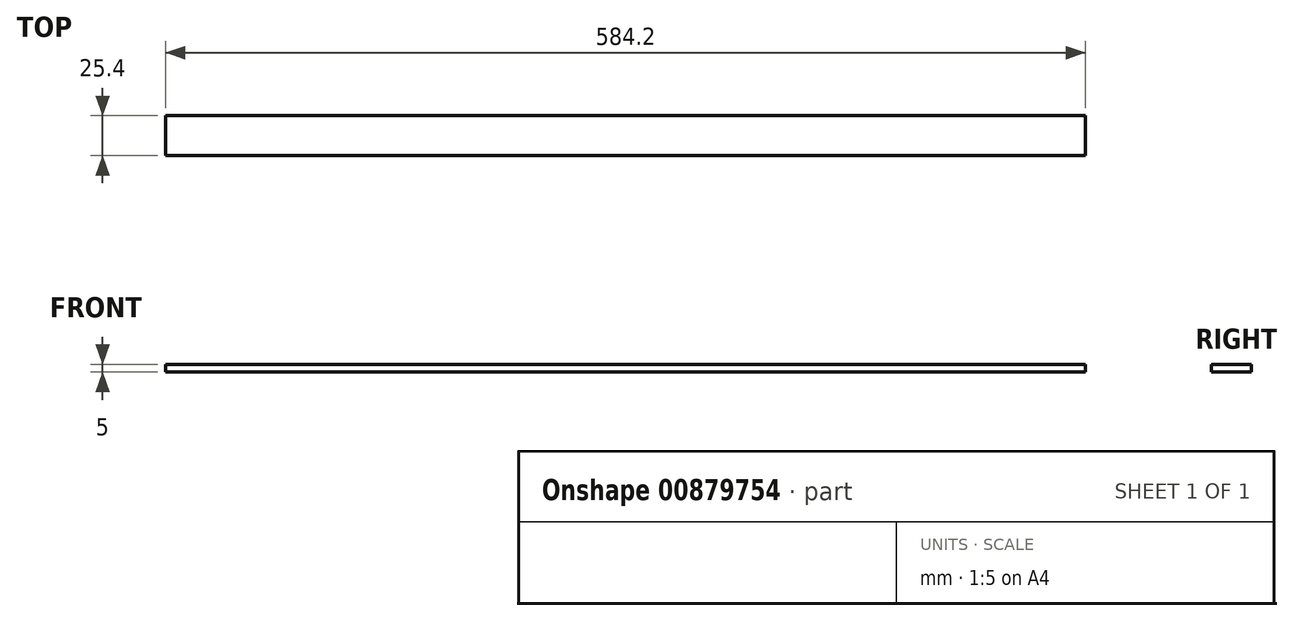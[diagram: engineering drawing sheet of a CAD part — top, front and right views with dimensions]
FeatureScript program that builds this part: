
annotation { "Feature Type Name" : "Feature", "Feature Type Description" : "" }
export const myFeature = defineFeature(function(context is Context, id is Id, definition is map)
    precondition{}
    {
        {
            var Q0;
            Q0=qCreatedBy(makeId("Front.planeOp"),FACE);
            var sketch = newSketch(context, id + "F0", { "sketchPlane" : qUnion([Q0])});
            skLineSegment(sketch, "E0.bottom", {"start": v(292.1, 2.5) * mm, "end": v(-292.1, 2.5) * mm});
            skLineSegment(sketch, "E0.top", {"start": v(292.1, -2.5) * mm, "end": v(-292.1, -2.5) * mm});
            skLineSegment(sketch, "E0.left", {"start": v(292.1, 2.5) * mm, "end": v(292.1, -2.5) * mm});
            skLineSegment(sketch, "E0.right", {"start": v(-292.1, 2.5) * mm, "end": v(-292.1, -2.5) * mm});
            skPoint(sketch, "E0.middle", {"position": v(0, 0) * mm});
            skSolve(sketch);
        }
        {
            var Q0;
            Q0 = qSketchRegion(id + "F0", true);
            extrude(context, id + "F1", {"entities" : qUnion([Q0]), "depth" : 25.4 * mm, "offsetDistance" : 25.4 * mm});
        }
    });
